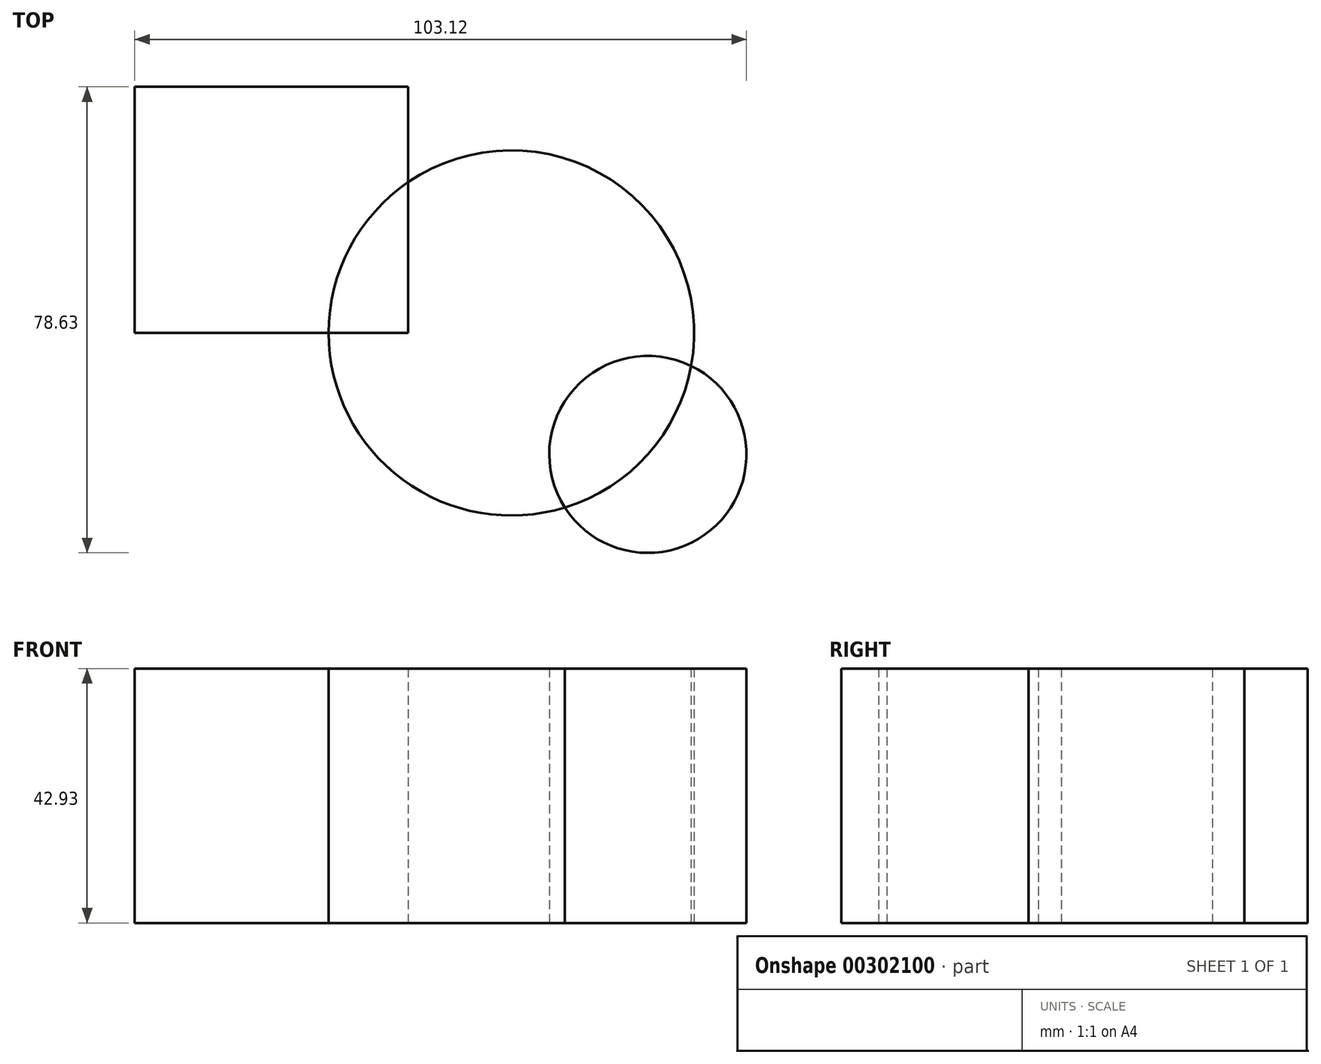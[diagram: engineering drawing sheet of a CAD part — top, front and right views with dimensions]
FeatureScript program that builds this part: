
annotation { "Feature Type Name" : "Feature", "Feature Type Description" : "" }
export const myFeature = defineFeature(function(context is Context, id is Id, definition is map)
    precondition{}
    {
        {
            var Q0;
            Q0=qCreatedBy(makeId("Top.planeOp"),FACE);
            var sketch = newSketch(context, id + "F0", { "sketchPlane" : qUnion([Q0])});
            skLineSegment(sketch, "E0.bottom", {"start": v(0, 0) * mm, "end": v(-46.12, 0) * mm});
            skLineSegment(sketch, "E0.top", {"start": v(0, 41.52) * mm, "end": v(-46.12, 41.52) * mm});
            skLineSegment(sketch, "E0.left", {"start": v(0, 0) * mm, "end": v(0, 41.52) * mm});
            skLineSegment(sketch, "E0.right", {"start": v(-46.12, 0) * mm, "end": v(-46.12, 41.52) * mm});
            skCircle(sketch, "E1", {"center": v(17.38, 0) * mm, "radius": 30.8 * mm});
            skCircle(sketch, "E2", {"center": v(40.38, -20.5) * mm, "radius": 16.62 * mm});
            skSolve(sketch);
        }
        {
            var Q0;
            {var subQ2=sQuery(id+"F0.wireOp",EDGE,"E0.top");Q0=makeQuery(id+"F0.imprint","IMPRINT",FACE,{"disambiguationData":[TD([[makeQuery(id+"F0.imprint","IMPRINT",EDGE,{"derivedFrom":subQ2}),1.0]])]});}
            var Q1;
            {var subQ0=sQuery(id+"F0.wireOp",EDGE,"E2");var subQ1=sQuery(id+"F0.wireOp",EDGE,"E1");var subQ2=makeQuery(id+"F0.imprint","INTERSECT",VERTEX,{"disambiguationData":[OD(0.0)],"derivedFrom":[subQ1,subQ0]});Q1=makeQuery(id+"F0.imprint","IMPRINT",FACE,{"disambiguationData":[TD([[makeQuery(id+"F0.imprint","IMPRINT",EDGE,{"disambiguationData":[TD([[subQ2,-1.0]])],"derivedFrom":subQ1}),-1.0]])]});}
            var Q2;
            {var subQ1=sQuery(id+"F0.wireOp",EDGE,"E0.left");var subQ5=sQuery(id+"F0.wireOp",EDGE,"E0.bottom");var subQ8=makeQuery(id+"F0.imprint","INTERSECT",VERTEX,{"derivedFrom":[subQ5,subQ1]});Q2=makeQuery(id+"F0.imprint","IMPRINT",FACE,{"disambiguationData":[TD([[makeQuery(id+"F0.imprint","IMPRINT",EDGE,{"disambiguationData":[TD([[subQ8,-1.0]])],"derivedFrom":subQ5}),1.0]])]});}
            extrude(context, id + "F1", {"entities" : qUnion([Q0, Q1, Q2]), "depth" : 42.93 * mm});
        }
    });
